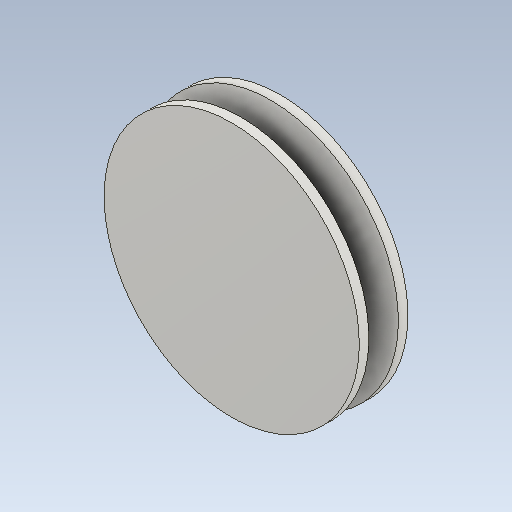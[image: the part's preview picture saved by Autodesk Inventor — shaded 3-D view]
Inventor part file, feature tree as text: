
AUTODESK INVENTOR PART (.ipt)
format: ipt  version: 2021 (Build 250183000, 183)  size: 137,216 bytes
history: native  units: mm (DEFAULTED — no unit token found)
features: other x3, fillet x2, pattern_linear x1
ambient origin geometry x8: Origin, YZ Plane, XZ Plane, XY Plane, X Axis, Y Axis, Z Axis, Center Point
bodies: Solid1 (feature_tree), Body (feature_tree)
feature tree (6):
  other  "Main Sketch"
  other  "Belt Plane"
  other  "Groove"
  fillet  "Fillet External"  Radius=8.5mm
  fillet  "Fillet Internal"  Radius=5.934119mm
  pattern_linear  "Groove Pattern"  Spacing1=2.0mm  [1 undecoded]
note: 1 required parameter value undecoded (feature->parameter linkage not recoverable at this tier; creation-order binding heuristic only, values carry confidence <= 0.55)
